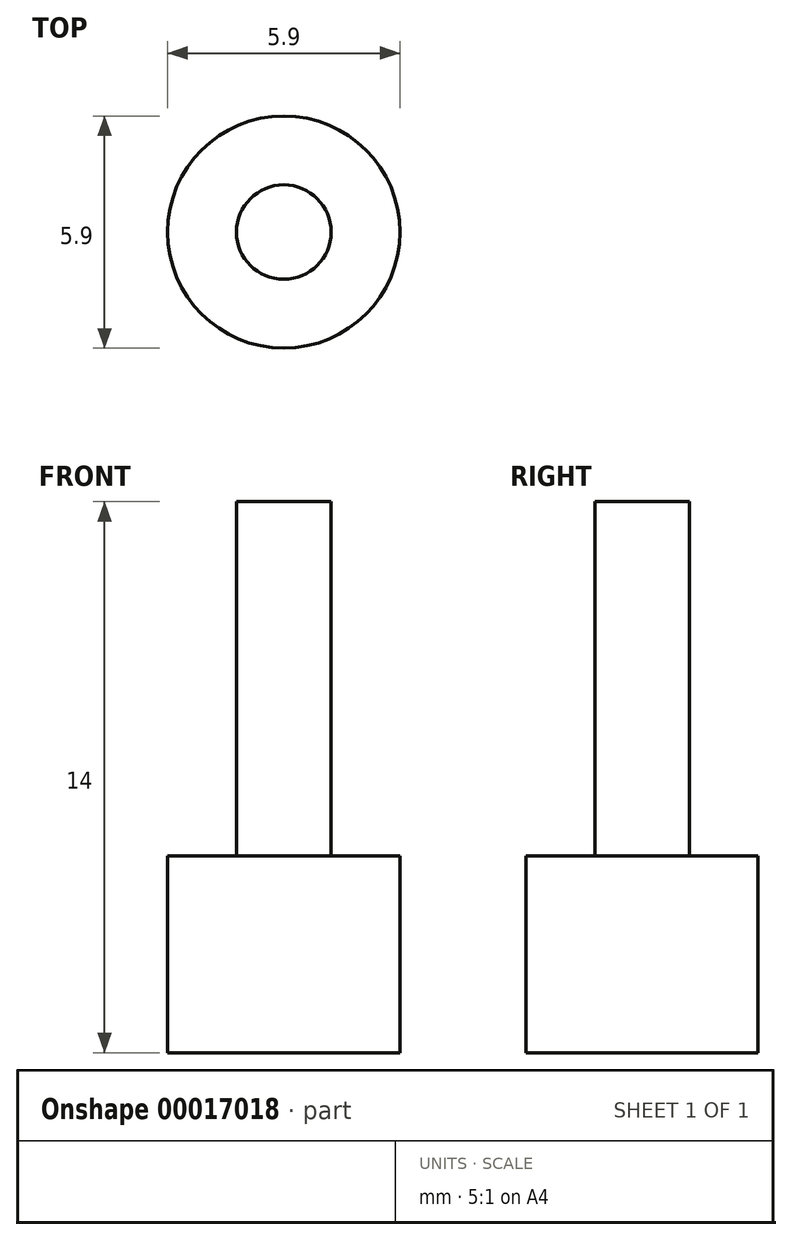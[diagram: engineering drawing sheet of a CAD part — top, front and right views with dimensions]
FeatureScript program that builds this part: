
annotation { "Feature Type Name" : "Feature", "Feature Type Description" : "" }
export const myFeature = defineFeature(function(context is Context, id is Id, definition is map)
    precondition{}
    {
        {
            var Q0;
            Q0=qCreatedBy(makeId("Top.planeOp"),FACE);
            var sketch = newSketch(context, id + "F0", { "sketchPlane" : qUnion([Q0])});
            skCircle(sketch, "E0", {"center": v(0, 0) * mm, "radius": 2.95 * mm});
            skSolve(sketch);
        }
        {
            var Q0;
            Q0 = qSketchRegion(id + "F0", true);
            extrude(context, id + "F1", {"entities" : qUnion([Q0]), "depth" : 5 * mm});
        }
        {
            var Q0;
            Q0=makeQuery(id+"F1.opExtrude","CAP_FACE",FACE,{"disambiguationData":[OSD([sQuery(id+"F0.wireOp",EDGE,"E0")])],"isStart":false});
            var sketch = newSketch(context, id + "F2", { "sketchPlane" : qUnion([Q0])});
            skCircle(sketch, "E1", {"center": v(0, 0) * mm, "radius": 1.2 * mm});
            skSolve(sketch);
        }
        {
            var Q0;
            Q0 = qSketchRegion(id + "F2", true);
            extrude(context, id + "F3", {"entities" : qUnion([Q0]), "operationType" : NewBodyOperationType.ADD, "depth" : 9 * mm});
        }
    });
